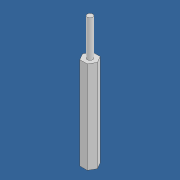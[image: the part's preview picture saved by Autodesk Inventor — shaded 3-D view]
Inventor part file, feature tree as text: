
AUTODESK INVENTOR PART (.ipt)
format: ipt  version: 2022.5 (Build 265521000, 521)  size: 92,160 bytes
history: native  units: mm
features: extrude x2, sketch x2, other x1
ambient origin geometry x8: Origin, YZ Plane, XZ Plane, XY Plane, X Axis, Y Axis, Z Axis, Center Point
bodies: Body1 (feature_tree)
feature tree (5):
  other  "實體1"
  extrude  "擠出1"  Depth=7.0mm
  extrude  "擠出2"  Depth=3.488mm
  sketch  "草圖1"
  sketch  "草圖2"
